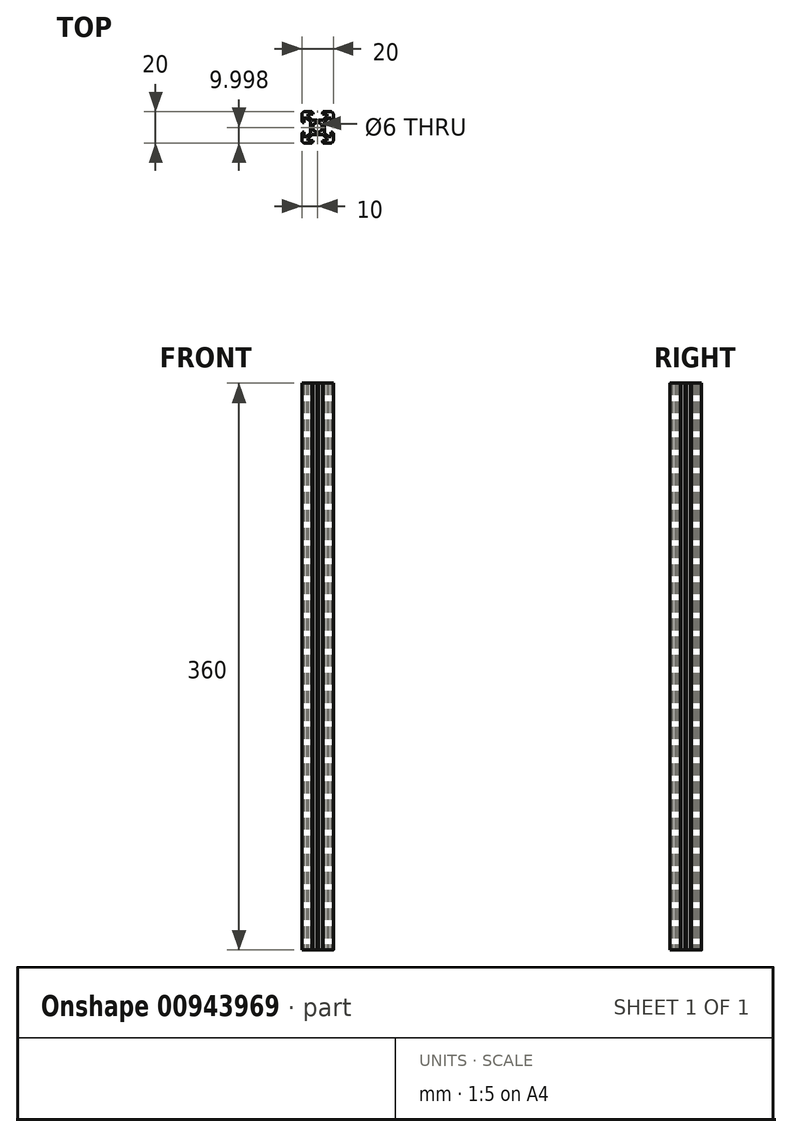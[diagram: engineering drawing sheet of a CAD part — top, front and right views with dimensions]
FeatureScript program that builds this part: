
annotation { "Feature Type Name" : "Feature", "Feature Type Description" : "" }
export const myFeature = defineFeature(function(context is Context, id is Id, definition is map)
    precondition{}
    {
        {
            var Q0;
            Q0=qCreatedBy(makeId("Top.planeOp"),FACE);
            var sketch = newSketch(context, id + "F0", { "sketchPlane" : qUnion([Q0])});
            skLineSegment(sketch, "E0.bottom", {"start": v(-8, -10) * mm, "end": v(8, -10) * mm});
            skLineSegment(sketch, "E0.top", {"start": v(-8, 10) * mm, "end": v(8, 10) * mm});
            skLineSegment(sketch, "E0.left", {"start": v(-10, -8) * mm, "end": v(-10, 8) * mm});
            skLineSegment(sketch, "E0.right", {"start": v(10, -8) * mm, "end": v(10, 8) * mm});
            skPoint(sketch, "E1.visualSharp", {"position": v(10, 10) * mm});
            skArc(sketch, "E1.filletArc", {"start": v(10, 8) * mm, "mid": v(9.41, 9.42) * mm, "end": v(8, 10) * mm});
            skPoint(sketch, "E2.visualSharp", {"position": v(-10, 10) * mm});
            skArc(sketch, "E2.filletArc", {"start": v(-8, 10) * mm, "mid": v(-9.41, 9.42) * mm, "end": v(-10, 8) * mm});
            skPoint(sketch, "E3.visualSharp", {"position": v(-10, -10) * mm});
            skArc(sketch, "E3.filletArc", {"start": v(-10, -8) * mm, "mid": v(-9.41, -9.4) * mm, "end": v(-8, -10) * mm});
            skPoint(sketch, "E4.visualSharp", {"position": v(10, -10) * mm});
            skArc(sketch, "E4.filletArc", {"start": v(8, -10) * mm, "mid": v(9.41, -9.4) * mm, "end": v(10, -8) * mm});
            skLineSegment(sketch, "E5", {"start": v(-10, -10) * mm, "end": v(10, 10) * mm, "construction": true});
            skLineSegment(sketch, "E6", {"start": v(-10, 10) * mm, "end": v(10, -10) * mm, "construction": true});
            skCircle(sketch, "E7", {"center": v(0, 0) * mm, "radius": 3 * mm});
            skCircle(sketch, "E8", {"center": v(0, 0) * mm, "radius": 2.75 * mm});
            skLineSegment(sketch, "E9.bottom", {"start": v(-2.45, -1.73) * mm, "end": v(-1.74, -2.44) * mm});
            skLineSegment(sketch, "E9.top", {"start": v(1.74, 2.45) * mm, "end": v(2.45, 1.75) * mm});
            skLineSegment(sketch, "E9.left", {"start": v(-2.45, -1.73) * mm, "end": v(1.74, 2.45) * mm});
            skLineSegment(sketch, "E9.right", {"start": v(-1.74, -2.44) * mm, "end": v(2.45, 1.75) * mm});
            skLineSegment(sketch, "E10.bottom", {"start": v(-2.45, 1.75) * mm, "end": v(-1.74, 2.45) * mm});
            skLineSegment(sketch, "E10.top", {"start": v(1.74, -2.44) * mm, "end": v(2.45, -1.73) * mm});
            skLineSegment(sketch, "E10.left", {"start": v(-2.45, 1.75) * mm, "end": v(1.74, -2.44) * mm});
            skLineSegment(sketch, "E10.right", {"start": v(-1.74, 2.45) * mm, "end": v(2.45, -1.73) * mm});
            skLineSegment(sketch, "E11", {"start": v(-3.5, 10) * mm, "end": v(-3.5, 9.5) * mm});
            skLineSegment(sketch, "E12", {"start": v(-3.5, 9.5) * mm, "end": v(-3, 9.5) * mm});
            skLineSegment(sketch, "E13", {"start": v(-3, 9.5) * mm, "end": v(-3, 8.5) * mm});
            skLineSegment(sketch, "E14", {"start": v(-3, 8.5) * mm, "end": v(-6, 8.5) * mm});
            skLineSegment(sketch, "E15", {"start": v(-6, 8.5) * mm, "end": v(-6, 7) * mm});
            skLineSegment(sketch, "E16", {"start": v(-3.5, 4.5) * mm, "end": v(-6, 7) * mm});
            skLineSegment(sketch, "E17", {"start": v(-3.5, 4.5) * mm, "end": v(3.5, 4.5) * mm});
            skLineSegment(sketch, "E18", {"start": v(3.5, 4.5) * mm, "end": v(6, 7) * mm});
            skLineSegment(sketch, "E19", {"start": v(6, 7) * mm, "end": v(6, 8.5) * mm});
            skLineSegment(sketch, "E20", {"start": v(6, 8.5) * mm, "end": v(3, 8.5) * mm});
            skLineSegment(sketch, "E21", {"start": v(3, 8.5) * mm, "end": v(3, 9.5) * mm});
            skLineSegment(sketch, "E22", {"start": v(3, 9.5) * mm, "end": v(3.5, 9.5) * mm});
            skLineSegment(sketch, "E23", {"start": v(3.5, 9.5) * mm, "end": v(3.5, 10) * mm});
            skLineSegment(sketch, "E24", {"start": v(0, 10) * mm, "end": v(0, -11.4) * mm, "construction": true});
            skLineSegment(sketch, "E25.1.0", {"start": v(-8.5, -6) * mm, "end": v(-7, -6) * mm});
            skLineSegment(sketch, "E25.1.1", {"start": v(-8.5, -3) * mm, "end": v(-8.5, -6) * mm});
            skLineSegment(sketch, "E25.1.2", {"start": v(-9.5, -3) * mm, "end": v(-8.5, -3) * mm});
            skLineSegment(sketch, "E25.1.3", {"start": v(-9.5, -3.5) * mm, "end": v(-9.5, -3) * mm});
            skLineSegment(sketch, "E25.1.4", {"start": v(-10, -3.5) * mm, "end": v(-9.5, -3.5) * mm});
            skLineSegment(sketch, "E25.1.5", {"start": v(-4.5, -3.5) * mm, "end": v(-7, -6) * mm});
            skLineSegment(sketch, "E25.1.6", {"start": v(-4.5, -3.5) * mm, "end": v(-4.5, 3.5) * mm});
            skLineSegment(sketch, "E25.1.7", {"start": v(-4.5, 3.5) * mm, "end": v(-7, 6) * mm});
            skLineSegment(sketch, "E25.1.8", {"start": v(-7, 6) * mm, "end": v(-8.5, 6) * mm});
            skLineSegment(sketch, "E25.1.9", {"start": v(-8.5, 6) * mm, "end": v(-8.5, 3) * mm});
            skLineSegment(sketch, "E25.1.10", {"start": v(-8.5, 3) * mm, "end": v(-9.5, 3) * mm});
            skLineSegment(sketch, "E25.1.11", {"start": v(-9.5, 3) * mm, "end": v(-9.5, 3.5) * mm});
            skLineSegment(sketch, "E25.1.12", {"start": v(-9.5, 3.5) * mm, "end": v(-10, 3.5) * mm});
            skLineSegment(sketch, "E25.2.0", {"start": v(6, -8.5) * mm, "end": v(6, -7) * mm});
            skLineSegment(sketch, "E25.2.1", {"start": v(3, -8.5) * mm, "end": v(6, -8.5) * mm});
            skLineSegment(sketch, "E25.2.2", {"start": v(3, -9.5) * mm, "end": v(3, -8.5) * mm});
            skLineSegment(sketch, "E25.2.3", {"start": v(3.5, -9.5) * mm, "end": v(3, -9.5) * mm});
            skLineSegment(sketch, "E25.2.4", {"start": v(3.5, -10) * mm, "end": v(3.5, -9.5) * mm});
            skLineSegment(sketch, "E25.2.5", {"start": v(3.5, -4.5) * mm, "end": v(6, -7) * mm});
            skLineSegment(sketch, "E25.2.6", {"start": v(3.5, -4.5) * mm, "end": v(-3.5, -4.5) * mm});
            skLineSegment(sketch, "E25.2.7", {"start": v(-3.5, -4.5) * mm, "end": v(-6, -7) * mm});
            skLineSegment(sketch, "E25.2.8", {"start": v(-6, -7) * mm, "end": v(-6, -8.5) * mm});
            skLineSegment(sketch, "E25.2.9", {"start": v(-6, -8.5) * mm, "end": v(-3, -8.5) * mm});
            skLineSegment(sketch, "E25.2.10", {"start": v(-3, -8.5) * mm, "end": v(-3, -9.5) * mm});
            skLineSegment(sketch, "E25.2.11", {"start": v(-3, -9.5) * mm, "end": v(-3.5, -9.5) * mm});
            skLineSegment(sketch, "E25.2.12", {"start": v(-3.5, -9.5) * mm, "end": v(-3.5, -10) * mm});
            skLineSegment(sketch, "E25.3.0", {"start": v(8.5, 6) * mm, "end": v(7, 6) * mm});
            skLineSegment(sketch, "E25.3.1", {"start": v(8.5, 3) * mm, "end": v(8.5, 6) * mm});
            skLineSegment(sketch, "E25.3.2", {"start": v(9.5, 3) * mm, "end": v(8.5, 3) * mm});
            skLineSegment(sketch, "E25.3.3", {"start": v(9.5, 3.5) * mm, "end": v(9.5, 3) * mm});
            skLineSegment(sketch, "E25.3.4", {"start": v(10, 3.5) * mm, "end": v(9.5, 3.5) * mm});
            skLineSegment(sketch, "E25.3.5", {"start": v(4.5, 3.5) * mm, "end": v(7, 6) * mm});
            skLineSegment(sketch, "E25.3.6", {"start": v(4.5, 3.5) * mm, "end": v(4.5, -3.5) * mm});
            skLineSegment(sketch, "E25.3.7", {"start": v(4.5, -3.5) * mm, "end": v(7, -6) * mm});
            skLineSegment(sketch, "E25.3.8", {"start": v(7, -6) * mm, "end": v(8.5, -6) * mm});
            skLineSegment(sketch, "E25.3.9", {"start": v(8.5, -6) * mm, "end": v(8.5, -3) * mm});
            skLineSegment(sketch, "E25.3.10", {"start": v(8.5, -3) * mm, "end": v(9.5, -3) * mm});
            skLineSegment(sketch, "E25.3.11", {"start": v(9.5, -3) * mm, "end": v(9.5, -3.5) * mm});
            skLineSegment(sketch, "E25.3.12", {"start": v(9.5, -3.5) * mm, "end": v(10, -3.5) * mm});
            skLineSegment(sketch, "E26", {"start": v(-0.5, 4.5) * mm, "end": v(0, 4) * mm});
            skLineSegment(sketch, "E27", {"start": v(0, 4) * mm, "end": v(0.5, 4.5) * mm});
            skLineSegment(sketch, "E28.1.0", {"start": v(-4, 0) * mm, "end": v(-4.5, 0.5) * mm});
            skLineSegment(sketch, "E28.1.1", {"start": v(-4.5, -0.5) * mm, "end": v(-4, 0) * mm});
            skLineSegment(sketch, "E28.2.0", {"start": v(0, -4) * mm, "end": v(-0.5, -4.5) * mm});
            skLineSegment(sketch, "E28.2.1", {"start": v(0.5, -4.5) * mm, "end": v(0, -4) * mm});
            skLineSegment(sketch, "E28.3.0", {"start": v(4, 0) * mm, "end": v(4.5, -0.5) * mm});
            skLineSegment(sketch, "E28.3.1", {"start": v(4.5, 0.5) * mm, "end": v(4, 0) * mm});
            skSolve(sketch);
        }
        {
            var Q0;
            {var subQ6=sQuery(id+"F0.wireOp",EDGE,"E1.filletArc");Q0=makeQuery(id+"F0.imprint","IMPRINT",FACE,{"disambiguationData":[TD([[makeQuery(id+"F0.imprint","IMPRINT",EDGE,{"derivedFrom":subQ6}),1.0]])]});}
            extrude(context, id + "F1", {"entities" : qUnion([Q0]), "depth" : 360 * mm, "offsetDistance" : 25.4 * mm});
        }
    });
